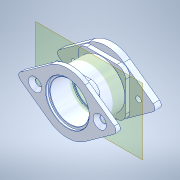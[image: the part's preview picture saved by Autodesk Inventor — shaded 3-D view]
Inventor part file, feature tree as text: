
AUTODESK INVENTOR PART (.ipt)
format: ipt  version: 2020 (Build 240168000, 168)  size: 228,352 bytes
history: native  units: in
note: dims shown in document units (in); Inventor stores cm internally (conversion verified against a paired STEP export)
features: other x2, plane x1
ambient origin geometry x8: Origin, YZ Plane, XZ Plane, XY Plane, X Axis, Y Axis, Z Axis, Center Point
bodies: Solid1 (feature_tree), Solid2 (feature_tree)
feature tree (3):
  plane  "Work Plane1"
  other  "217-3436-001 Rev2_1:1"
  other  "217-3436-002 Rev2_2:1"
